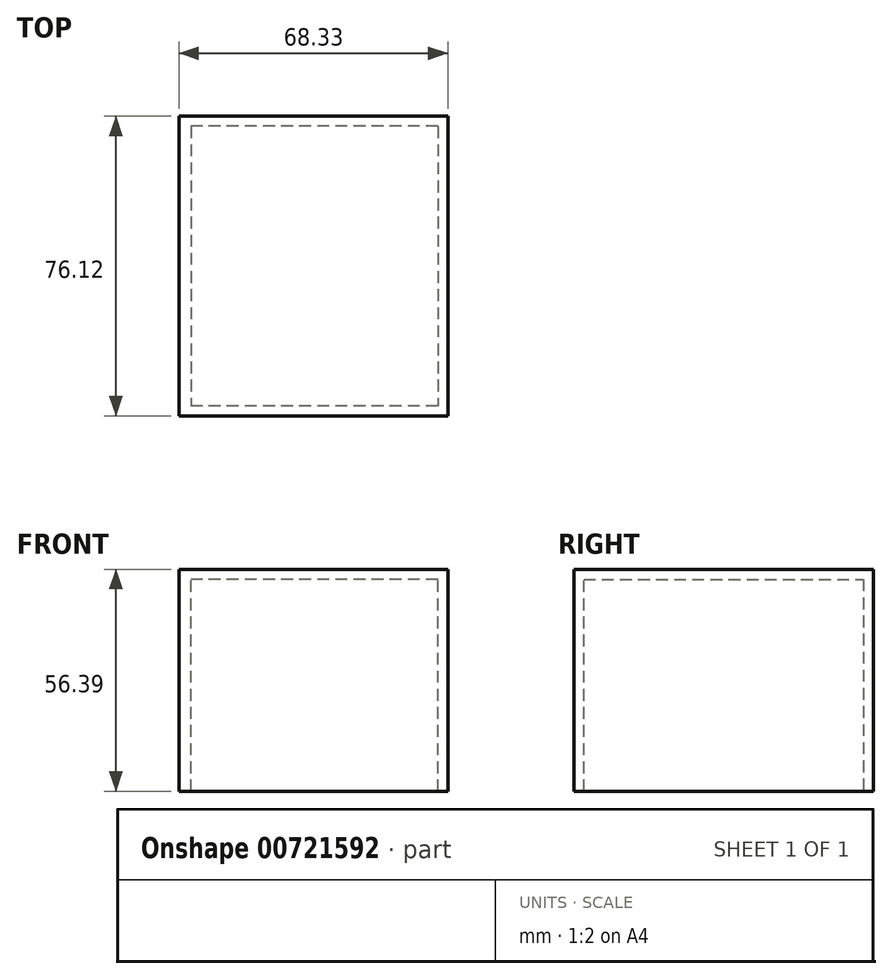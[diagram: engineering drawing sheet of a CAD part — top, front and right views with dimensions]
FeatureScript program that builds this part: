
annotation { "Feature Type Name" : "Feature", "Feature Type Description" : "" }
export const myFeature = defineFeature(function(context is Context, id is Id, definition is map)
    precondition{}
    {
        {
            var Q0;
            Q0=qCreatedBy(makeId("Right.planeOp"),FACE);
            var sketch = newSketch(context, id + "F0", { "sketchPlane" : qUnion([Q0])});
            skLineSegment(sketch, "E0", {"start": v(0, 56.39) * mm, "end": v(76.12, 56.39) * mm});
            skLineSegment(sketch, "E1", {"start": v(76.12, 56.39) * mm, "end": v(76.12, 0) * mm});
            skLineSegment(sketch, "E2", {"start": v(76.12, 0) * mm, "end": v(0, 0) * mm});
            skLineSegment(sketch, "E3", {"start": v(0, 0) * mm, "end": v(0, 56.39) * mm});
            skSolve(sketch);
        }
        {
            var Q0;
            Q0=makeQuery(id+"F0.imprint","IMPRINT",FACE,{"disambiguationData":[TD([[makeQuery(id+"F0.imprint","IMPRINT",EDGE,{"derivedFrom":sQuery(id+"F0.wireOp",EDGE,"E0")}),-1.0]])]});
            extrude(context, id + "F1", {"entities" : qUnion([Q0]), "depth" : 67.82 * mm, "offsetDistance" : 25.4 * mm});
        }
        {
            var Q0;
            Q0=makeQuery(id+"F1.opExtrude","SWEPT_FACE",FACE,{"disambiguationData":[OSD([sQuery(id+"F0.wireOp",EDGE,"E3")])]});
            var sketch = newSketch(context, id + "F2", { "sketchPlane" : qUnion([Q0])});
            skLineSegment(sketch, "E4.bottom", {"start": v(24.35, 0) * mm, "end": v(42.27, 0) * mm});
            skLineSegment(sketch, "E4.top", {"start": v(24.35, 17.29) * mm, "end": v(42.27, 17.29) * mm});
            skLineSegment(sketch, "E4.left", {"start": v(24.35, 0) * mm, "end": v(24.35, 17.29) * mm});
            skLineSegment(sketch, "E4.right", {"start": v(42.27, 0) * mm, "end": v(42.27, 17.29) * mm});
            skSolve(sketch);
        }
        {
            var Q0;
            Q0=makeQuery(id+"F2.imprint","IMPRINT",FACE,{"disambiguationData":[TD([[makeQuery(id+"F2.imprint","IMPRINT",EDGE,{"derivedFrom":sQuery(id+"F2.wireOp",EDGE,"E4.bottom")}),-1.0]])]});
            extrude(context, id + "F3", {"entities" : qUnion([Q0]), "operationType" : NewBodyOperationType.ADD, "oppositeDirection" : true, "depth" : 66.8 * mm, "offsetDistance" : 25.4 * mm});
        }
        {
            var Q0;
            Q0=makeQuery(id+"F1.opExtrude","SWEPT_FACE",FACE,{"disambiguationData":[OSD([sQuery(id+"F0.wireOp",EDGE,"E2")])]});
            shell(context, id + "F4", {"entities" : qUnion([Q0]), "thickness" : 2.54 * mm});
        }
        {
            var Q0;
            Q0=makeQuery(id+"F1.opExtrude","CAP_FACE",FACE,{"disambiguationData":[OSD([sQuery(id+"F0.wireOp",EDGE,"E0"),sQuery(id+"F0.wireOp",EDGE,"E1"),sQuery(id+"F0.wireOp",EDGE,"E2"),sQuery(id+"F0.wireOp",EDGE,"E3")])],"isStart":false});
            var sketch = newSketch(context, id + "F5", { "sketchPlane" : qUnion([Q0])});
            skLineSegment(sketch, "E5.bottom", {"start": v(26.49, 0) * mm, "end": v(44.02, 0) * mm});
            skLineSegment(sketch, "E5.top", {"start": v(26.49, 13.12) * mm, "end": v(44.02, 13.12) * mm});
            skLineSegment(sketch, "E5.left", {"start": v(26.49, 0) * mm, "end": v(26.49, 13.12) * mm});
            skLineSegment(sketch, "E5.right", {"start": v(44.02, 0) * mm, "end": v(44.02, 13.12) * mm});
            skSolve(sketch);
        }
        {
            var Q0;
            Q0 = qSketchRegion(id + "F5", true);
            var Q1;
            Q1=makeQuery(id+"F1.opExtrude","CAP_FACE",FACE,{"disambiguationData":[OSD([sQuery(id+"F0.wireOp",EDGE,"E0"),sQuery(id+"F0.wireOp",EDGE,"E1"),sQuery(id+"F0.wireOp",EDGE,"E2"),sQuery(id+"F0.wireOp",EDGE,"E3")])],"isStart":true});
            extrude(context, id + "F6", {"entities" : qUnion([Q0, Q1]), "operationType" : NewBodyOperationType.ADD, "oppositeDirection" : true, "depth" : 0.5 * mm, "offsetDistance" : 25.4 * mm});
        }
    });
